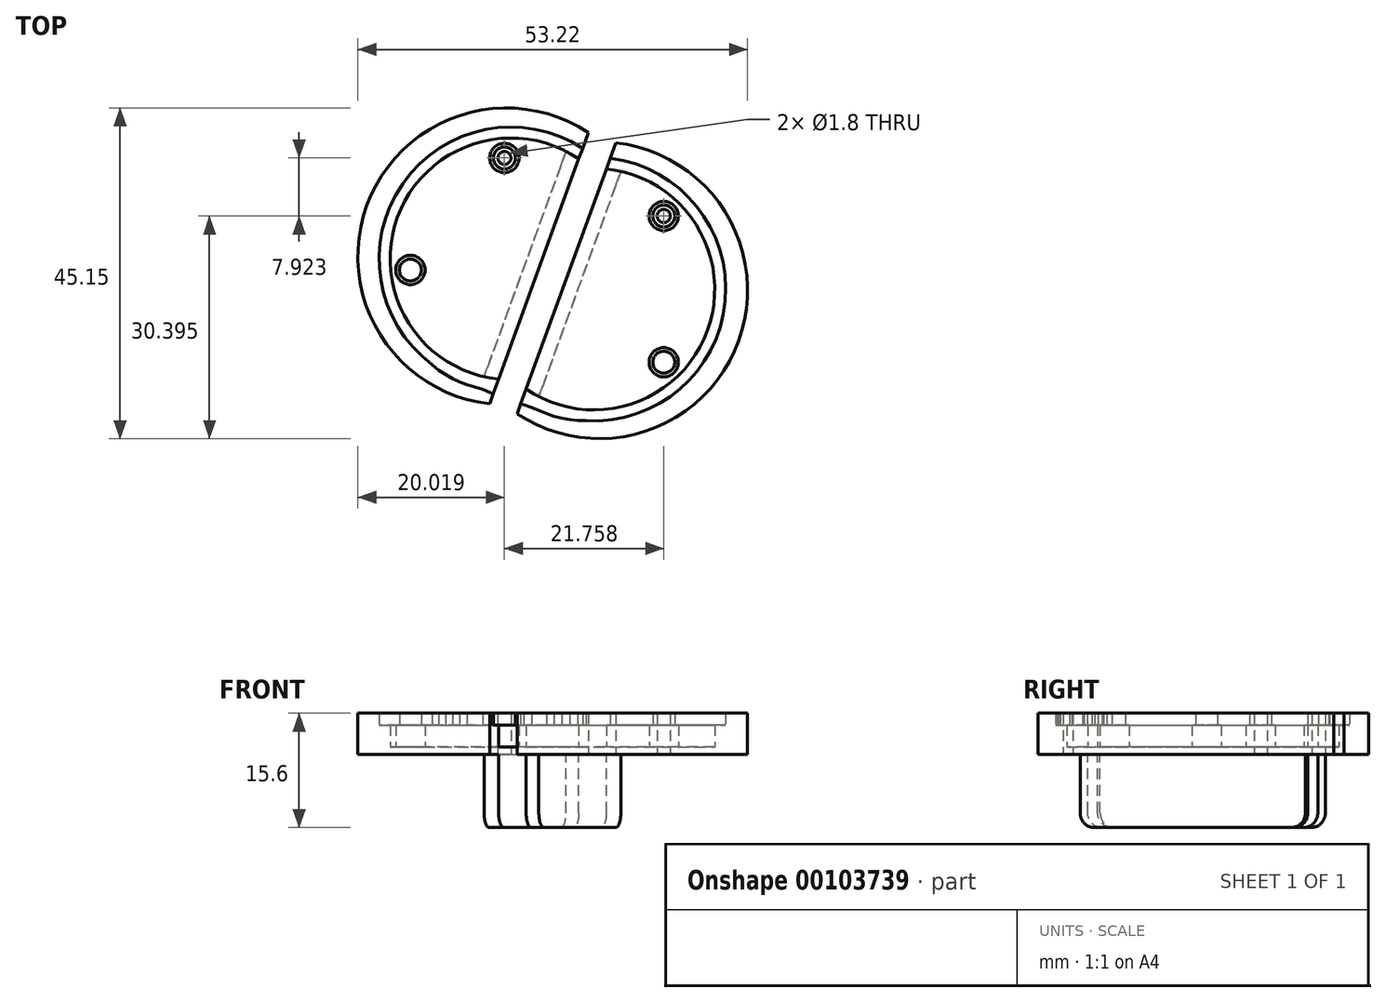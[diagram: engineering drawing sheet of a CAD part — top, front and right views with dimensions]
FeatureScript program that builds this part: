
annotation { "Feature Type Name" : "Feature", "Feature Type Description" : "" }
export const myFeature = defineFeature(function(context is Context, id is Id, definition is map)
    precondition{}
    {
        {
            assignVariable(context, id + "F0", {"name" : "pcb_height", "anyValue" : 1.6});
        }
        {
            assignVariable(context, id + "F1", {"name" : "spacer_height", "anyValue" : 3});
        }
        {
            assignVariable(context, id + "F2", {"name" : "bottom_height", "anyValue" : 1});
        }
        {
            var Q0;
            Q0=qCreatedBy(makeId("Top.planeOp"),FACE);
            var sketch = newSketch(context, id + "F3", { "sketchPlane" : qUnion([Q0])});
            skCircle(sketch, "E0", {"center": v(41.5, 9.99) * mm, "radius": 1.5 * mm});
            skCircle(sketch, "E1", {"center": v(41.5, -9.98) * mm, "radius": 1.5 * mm});
            skArc(sketch, "E2", {"start": v(30.9, -17.96) * mm, "mid": v(49.9, -1.64) * mm, "end": v(34.19, 17.87) * mm});
            skCircle(sketch, "E3", {"center": v(41.5, 9.99) * mm, "radius": 2 * mm});
            skCircle(sketch, "E4", {"center": v(41.5, -9.98) * mm, "radius": 2 * mm});
            skArc(sketch, "E5", {"start": v(22.7, -13.64) * mm, "mid": v(47.47, -5.64) * mm, "end": v(33.66, 16.42) * mm});
            skLineSegment(sketch, "E6.trimOffspring", {"start": v(34.19, 17.87) * mm, "end": v(22.7, -13.64) * mm});
            skLineSegment(sketch, "E7", {"start": v(34.19, 17.87) * mm, "end": v(34.96, 19.99) * mm});
            skArc(sketch, "E8.trimOffspring", {"start": v(21.48, -17.02) * mm, "mid": v(51.73, -7.08) * mm, "end": v(34.96, 19.99) * mm});
            skLineSegment(sketch, "E9", {"start": v(35.65, 16.1) * mm, "end": v(24.44, -14.67) * mm});
            skLineSegment(sketch, "E10", {"start": v(30.9, -17.96) * mm, "end": v(29.75, -17.96) * mm});
            skLineSegment(sketch, "E11", {"start": v(29.75, -17.96) * mm, "end": v(28.64, -17.84) * mm});
            skLineSegment(sketch, "E12", {"start": v(28.64, -17.84) * mm, "end": v(27.58, -17.64) * mm});
            skLineSegment(sketch, "E13", {"start": v(27.58, -17.64) * mm, "end": v(26.54, -17.36) * mm});
            skLineSegment(sketch, "E14", {"start": v(26.54, -17.36) * mm, "end": v(25.49, -17) * mm});
            skLineSegment(sketch, "E15", {"start": v(25.49, -17) * mm, "end": v(23.45, -16.14) * mm});
            skLineSegment(sketch, "E16", {"start": v(23.45, -16.14) * mm, "end": v(22.4, -15.78) * mm});
            skLineSegment(sketch, "E17", {"start": v(22.4, -15.78) * mm, "end": v(21.96, -15.69) * mm});
            skLineSegment(sketch, "E18", {"start": v(22.7, -13.64) * mm, "end": v(21.96, -15.69) * mm});
            skLineSegment(sketch, "E19", {"start": v(21.96, -15.69) * mm, "end": v(21.48, -17.02) * mm});
            skCircle(sketch, "E20", {"center": v(41.5, 9.99) * mm, "radius": 0.9 * mm});
            skSolve(sketch);
        }
        {
            var Q0;
            Q0=makeQuery(id+"F3.imprint","IMPRINT",FACE,{"disambiguationData":[TD([[makeQuery(id+"F3.imprint","IMPRINT",EDGE,{"derivedFrom":sQuery(id+"F3.wireOp",EDGE,"E3")}),-1.0]])]});
            var Q1;
            {var subQ3=sQuery(id+"F3.wireOp",EDGE,"E9");Q1=makeQuery(id+"F3.imprint","IMPRINT",FACE,{"disambiguationData":[TD([[makeQuery(id+"F3.imprint","IMPRINT",EDGE,{"derivedFrom":subQ3}),-1.0]])]});}
            extrude(context, id + "F4", {"entities" : qUnion([Q0, Q1]), "depth" : (getVariable(context, 'bottom_height')) * mm});
        }
        {
            var Q0;
            {var subQ1=sQuery(id+"F3.wireOp",EDGE,"E2");var subQ3=sQuery(id+"F3.wireOp",EDGE,"XkVqvH0T-IIrr-ZfkP-ho6W-M6DpgLbPDYoE");var subQ4=makeQuery(id+"F3.imprint","INTERSECT",VERTEX,{"derivedFrom":[subQ1,subQ3]});Q0=makeQuery(id+"F3.imprint","IMPRINT",FACE,{"disambiguationData":[TD([[makeQuery(id+"F3.imprint","IMPRINT",EDGE,{"disambiguationData":[TD([[subQ4,-1.0]])],"derivedFrom":subQ1}),1.0]])]});}
            var Q1;
            {var subQ0=sQuery(id+"F3.wireOp",EDGE,"E10");Q1=makeQuery(id+"F3.imprint","IMPRINT",FACE,{"disambiguationData":[TD([[makeQuery(id+"F3.imprint","IMPRINT",EDGE,{"derivedFrom":subQ0}),-1.0]])]});}
            var Q2;
            Q2=makeQuery(id+"F3.imprint","IMPRINT",FACE,{"disambiguationData":[TD([[makeQuery(id+"F3.imprint","IMPRINT",EDGE,{"derivedFrom":sQuery(id+"F3.wireOp",EDGE,"E1")}),-1.0]])]});
            var Q3;
            Q3=makeQuery(id+"F3.imprint","IMPRINT",FACE,{"disambiguationData":[TD([[makeQuery(id+"F3.imprint","IMPRINT",EDGE,{"derivedFrom":sQuery(id+"F3.wireOp",EDGE,"E0")}),-1.0]])]});
            extrude(context, id + "F5", {"entities" : qUnion([Q0, Q1, Q2, Q3]), "operationType" : NewBodyOperationType.ADD, "depth" : (getVariable(context, 'bottom_height') + getVariable(context, 'spacer_height')) * mm});
        }
        {
            var Q0;
            Q0=makeQuery(id+"F3.imprint","IMPRINT",FACE,{"disambiguationData":[TD([[makeQuery(id+"F3.imprint","IMPRINT",EDGE,{"derivedFrom":sQuery(id+"F3.wireOp",EDGE,"E2")}),-1.0]])]});
            var Q1;
            {var subQ0=sQuery(id+"F3.wireOp",EDGE,"YtyEXGQq-l3uL-UiFC-b7lW-DGPdYCoiLaOQ");Q1=makeQuery(id+"F3.imprint","IMPRINT",FACE,{"disambiguationData":[TD([[makeQuery(id+"F3.imprint","IMPRINT",EDGE,{"derivedFrom":subQ0}),1.0]])]});}
            var Q2;
            {var subQ0=sQuery(id+"F3.wireOp",EDGE,"j1vpeVGi-3Wjd-c7q3-rXIW-uE4deMf4NGZI");Q2=makeQuery(id+"F3.imprint","IMPRINT",FACE,{"disambiguationData":[TD([[makeQuery(id+"F3.imprint","IMPRINT",EDGE,{"derivedFrom":subQ0}),-1.0]])]});}
            var Q3;
            {var subQ4=sQuery(id+"F3.wireOp",EDGE,"4hLh4N7H-PqiM-gMYx-UIys-RkK7pKbqzVCS");Q3=makeQuery(id+"F3.imprint","IMPRINT",FACE,{"disambiguationData":[TD([[makeQuery(id+"F3.imprint","IMPRINT",EDGE,{"derivedFrom":subQ4}),1.0]])]});}
            var Q4;
            {var subQ3=sQuery(id+"F3.wireOp",EDGE,"E7");Q4=makeQuery(id+"F3.imprint","IMPRINT",FACE,{"disambiguationData":[TD([[makeQuery(id+"F3.imprint","IMPRINT",EDGE,{"derivedFrom":subQ3}),1.0]])]});}
            var Q5;
            Q5=makeQuery(id+"F3.imprint","IMPRINT",FACE,{"disambiguationData":[TD([[makeQuery(id+"F3.imprint","IMPRINT",EDGE,{"derivedFrom":sQuery(id+"F3.wireOp",EDGE,"E1")}),1.0]])]});
            var Q6;
            Q6=makeQuery(id+"F3.imprint","IMPRINT",FACE,{"disambiguationData":[TD([[makeQuery(id+"F3.imprint","IMPRINT",EDGE,{"derivedFrom":sQuery(id+"F3.wireOp",EDGE,"E0")}),1.0]])]});
            extrude(context, id + "F6", {"entities" : qUnion([Q0, Q1, Q2, Q3, Q4, Q5, Q6]), "operationType" : NewBodyOperationType.ADD, "depth" : (getVariable(context, 'bottom_height') + getVariable(context, 'spacer_height') + getVariable(context, 'pcb_height')) * mm});
        }
        {
            var Q0;
            {var subQ3=sQuery(id+"F3.wireOp",EDGE,"E9");Q0=makeQuery(id+"F3.imprint","IMPRINT",FACE,{"disambiguationData":[TD([[makeQuery(id+"F3.imprint","IMPRINT",EDGE,{"derivedFrom":subQ3}),-1.0]])]});}
            extrude(context, id + "F7", {"entities" : qUnion([Q0]), "operationType" : NewBodyOperationType.ADD, "oppositeDirection" : true, "depth" : 10 * mm});
        }
        {
            var Q0;
            {var subQ0=sQuery(id+"F3.wireOp",EDGE,"E5");Q0=makeQuery(id+"F7.opExtrude","CAP_EDGE",EDGE,{"disambiguationData":[OSD([subQ0]),TDD([makeQuery(id+"F3.imprint","IMPRINT",EDGE,{"disambiguationData":[TD([[makeQuery(id+"F3.imprint","INTERSECT",VERTEX,{"derivedFrom":[subQ0,sQuery(id+"F3.wireOp",EDGE,"E6.trimOffspring")]}),1.0]])],"derivedFrom":subQ0})])],"isStart":false});}
            var Q1;
            {var subQ0=sQuery(id+"F3.wireOp",EDGE,"E5");Q1=makeQuery(id+"F7.opExtrude","CAP_EDGE",EDGE,{"disambiguationData":[OSD([subQ0]),TDD([makeQuery(id+"F3.imprint","IMPRINT",EDGE,{"disambiguationData":[TD([[makeQuery(id+"F3.imprint","INTERSECT",VERTEX,{"disambiguationData":[OD(1.0)],"derivedFrom":[subQ0,sQuery(id+"F3.wireOp",EDGE,"E9")]}),1.0]])],"derivedFrom":subQ0})])],"isStart":false});}
            fillet(context, id + "F8", {"entities" : qUnion([Q0, Q1]), "radius" : 2 * mm, "tangentPropagation" : true, "allowEdgeOverflow" : false});
        }
        {
            var Q0;
            {var subQ0=sQuery(id+"F3.wireOp",EDGE,"E6.trimOffspring");Q0=makeQuery(id+"F7.boolean.opBoolean","MERGE",FACE,{"derivedFrom":[makeQuery(id+"F6.boolean.opBoolean","MERGE",FACE,{"derivedFrom":[makeQuery(id+"F5.boolean.opBoolean","MERGE",FACE,{"derivedFrom":[makeQuery(id+"F4.opExtrude","SWEPT_FACE",FACE,{"disambiguationData":[OSD([subQ0])]}),makeQuery(id+"F5.opExtrude","SWEPT_FACE",FACE,{"disambiguationData":[OSD([subQ0])]}),makeQuery(id+"F5.opExtrude","SWEPT_FACE",FACE,{"disambiguationData":[OSD([sQuery(id+"F3.wireOp",EDGE,"E18")])]})]}),makeQuery(id+"F6.opExtrude","SWEPT_FACE",FACE,{"disambiguationData":[OSD([sQuery(id+"F3.wireOp",EDGE,"E7")])]}),makeQuery(id+"F6.opExtrude","SWEPT_FACE",FACE,{"disambiguationData":[OSD([sQuery(id+"F3.wireOp",EDGE,"E19")])]})]}),makeQuery(id+"F7.opExtrude","SWEPT_FACE",FACE,{"disambiguationData":[OSD([subQ0])]})]});}
            cPlane(context, id + "F9", {"entities" : qUnion([Q0]), "cplaneType" : CPlaneType.OFFSET, "offset" : 2 * mm, "width" : 150 * mm, "height" : 150 * mm});
        }
        {
            var Q0;
            Q0=makeQuery(id+"F4.opExtrude","SWEPT_BODY",BODY,{"disambiguationData":[OSD([sQuery(id+"F3.wireOp",EDGE,"E3"),sQuery(id+"F3.wireOp",EDGE,"dfRvWslK-FhLC-aZRQ-BsVm-TQMV6JwteC68"),sQuery(id+"F3.wireOp",EDGE,"E4"),sQuery(id+"F3.wireOp",EDGE,"E5"),sQuery(id+"F3.wireOp",EDGE,"bCT80wSM-Ikjn-8lyl-vL5o-bz4jRUpXxg8L"),sQuery(id+"F3.wireOp",EDGE,"jbnTmvST-mwhj-ACoZ-QXGy-Fn6N0akZmLyV")])]});
            var Q1;
            Q1=qCreatedBy(id+"F9.planeOp",FACE);
            mirror(context, id + "F10", {"entities" : qUnion([Q0]), "mirrorPlane" : qUnion([Q1])});
        }
    });
